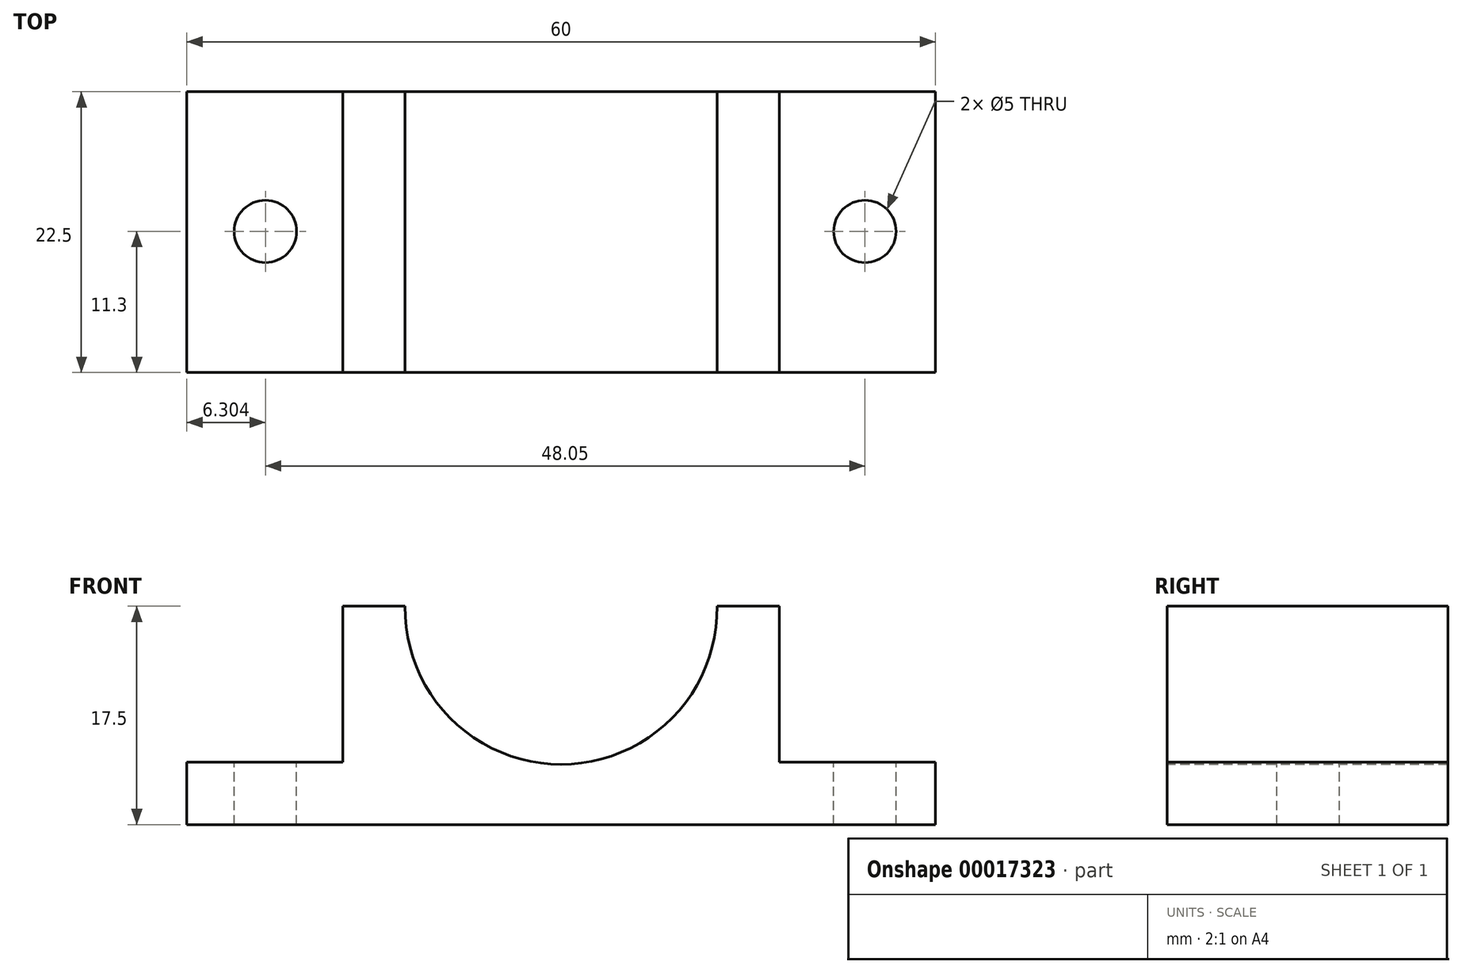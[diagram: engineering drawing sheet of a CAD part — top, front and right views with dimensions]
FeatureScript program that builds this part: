
annotation { "Feature Type Name" : "Feature", "Feature Type Description" : "" }
export const myFeature = defineFeature(function(context is Context, id is Id, definition is map)
    precondition{}
    {
        {
            var Q0;
            Q0=qCreatedBy(makeId("Front.planeOp"),FACE);
            var sketch = newSketch(context, id + "F0", { "sketchPlane" : qUnion([Q0])});
            skLineSegment(sketch, "E0", {"start": v(-31.4, -37.87) * mm, "end": v(28.6, -37.87) * mm});
            skLineSegment(sketch, "E1", {"start": v(-31.4, -37.87) * mm, "end": v(-31.4, -32.87) * mm});
            skLineSegment(sketch, "E2", {"start": v(28.6, -37.87) * mm, "end": v(28.6, -32.87) * mm});
            skLineSegment(sketch, "E3", {"start": v(28.6, -32.87) * mm, "end": v(16.1, -32.87) * mm});
            skLineSegment(sketch, "E4", {"start": v(-31.4, -32.87) * mm, "end": v(-18.9, -32.87) * mm});
            skLineSegment(sketch, "E5", {"start": v(-18.9, -32.87) * mm, "end": v(-18.9, -20.37) * mm});
            skLineSegment(sketch, "E6", {"start": v(16.1, -32.87) * mm, "end": v(16.1, -20.37) * mm});
            skLineSegment(sketch, "E7", {"start": v(16.1, -20.37) * mm, "end": v(11.1, -20.37) * mm});
            skLineSegment(sketch, "E8", {"start": v(-18.9, -20.37) * mm, "end": v(-13.9, -20.37) * mm});
            skArc(sketch, "E9", {"start": v(-13.9, -20.37) * mm, "mid": v(-1.4, -33.05) * mm, "end": v(11.1, -20.37) * mm});
            skSolve(sketch);
        }
        {
            var Q0;
            Q0=makeQuery(id+"F0.imprint","IMPRINT",FACE,{"disambiguationData":[TD([[makeQuery(id+"F0.imprint","IMPRINT",EDGE,{"derivedFrom":sQuery(id+"F0.wireOp",EDGE,"E0")}),1.0]])]});
            extrude(context, id + "F1", {"entities" : qUnion([Q0]), "oppositeDirection" : true, "depth" : 22.5 * mm});
        }
        {
            var Q0;
            Q0=makeQuery(id+"F1.opExtrude","SWEPT_FACE",FACE,{"disambiguationData":[OSD([sQuery(id+"F0.wireOp",EDGE,"E3")])]});
            var sketch = newSketch(context, id + "F2", { "sketchPlane" : qUnion([Q0])});
            skPoint(sketch, "E10", {"position": v(25.45, 11.3) * mm});
            skPoint(sketch, "E11", {"position": v(22.95, 11.3) * mm});
            skSolve(sketch);
        }
        {
            var Q0;
            Q0=sQuery(id+"F2.wireOp",VERTEX,"E11");
            var Q1;
            Q1=makeQuery(id+"F1.opExtrude","SWEPT_BODY",BODY,{"disambiguationData":[OSD([sQuery(id+"F0.wireOp",EDGE,"E0"),sQuery(id+"F0.wireOp",EDGE,"E1"),sQuery(id+"F0.wireOp",EDGE,"E2"),sQuery(id+"F0.wireOp",EDGE,"E3"),sQuery(id+"F0.wireOp",EDGE,"E4"),sQuery(id+"F0.wireOp",EDGE,"E5"),sQuery(id+"F0.wireOp",EDGE,"E6"),sQuery(id+"F0.wireOp",EDGE,"E7"),sQuery(id+"F0.wireOp",EDGE,"E8"),sQuery(id+"F0.wireOp",EDGE,"E9")])]});
            hole(context, id + "F3", {"style" : HoleStyle.SIMPLE, "holeDiameter" : 5 * mm, "endStyle" : HoleEndStyle.THROUGH, "locations" : qUnion([Q0]), "scope" : qUnion([Q1])});
        }
        {
            var Q0;
            Q0=makeQuery(id+"F1.opExtrude","SWEPT_FACE",FACE,{"disambiguationData":[OSD([sQuery(id+"F0.wireOp",EDGE,"E4")])]});
            var sketch = newSketch(context, id + "F4", { "sketchPlane" : qUnion([Q0])});
            skPoint(sketch, "E12", {"position": v(-25.1, 11.3) * mm});
            skSolve(sketch);
        }
        {
            var Q0;
            Q0=sQuery(id+"F4.wireOp",VERTEX,"E12");
            var Q1;
            Q1=makeQuery(id+"F1.opExtrude","SWEPT_BODY",BODY,{"disambiguationData":[OSD([sQuery(id+"F0.wireOp",EDGE,"E0"),sQuery(id+"F0.wireOp",EDGE,"E1"),sQuery(id+"F0.wireOp",EDGE,"E2"),sQuery(id+"F0.wireOp",EDGE,"E3"),sQuery(id+"F0.wireOp",EDGE,"E4"),sQuery(id+"F0.wireOp",EDGE,"E5"),sQuery(id+"F0.wireOp",EDGE,"E6"),sQuery(id+"F0.wireOp",EDGE,"E7"),sQuery(id+"F0.wireOp",EDGE,"E8"),sQuery(id+"F0.wireOp",EDGE,"E9")])]});
            hole(context, id + "F5", {"style" : HoleStyle.SIMPLE, "holeDiameter" : 5 * mm, "endStyle" : HoleEndStyle.THROUGH, "locations" : qUnion([Q0]), "scope" : qUnion([Q1])});
        }
    });
